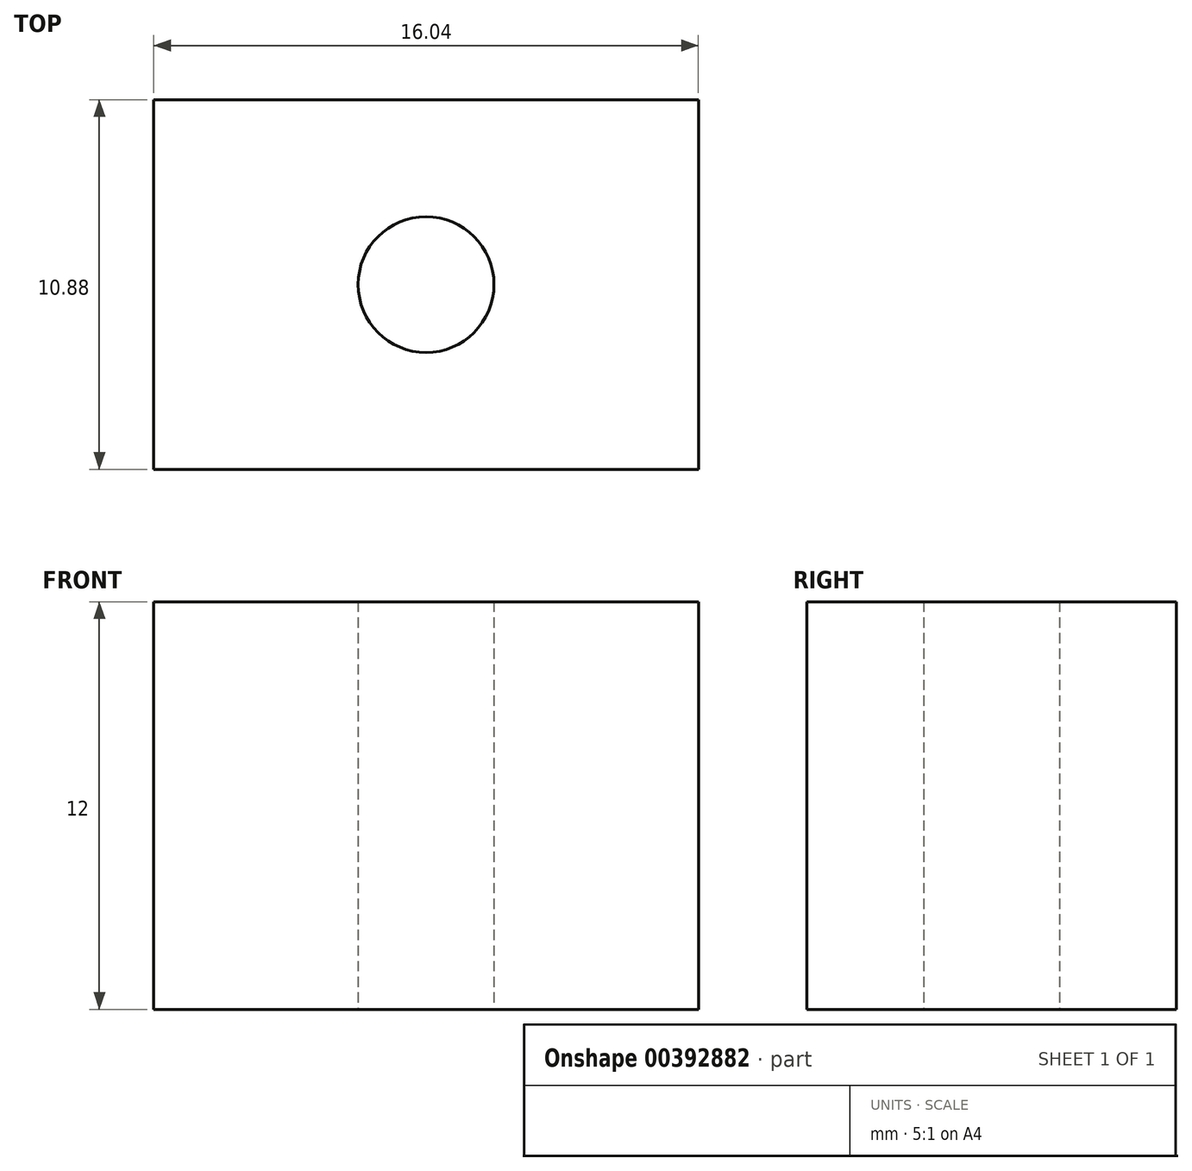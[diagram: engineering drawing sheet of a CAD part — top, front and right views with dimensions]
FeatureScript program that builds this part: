
annotation { "Feature Type Name" : "Feature", "Feature Type Description" : "" }
export const myFeature = defineFeature(function(context is Context, id is Id, definition is map)
    precondition{}
    {
        {
            var Q0;
            Q0=qCreatedBy(makeId("Top.planeOp"),FACE);
            var sketch = newSketch(context, id + "F0", { "sketchPlane" : qUnion([Q0])});
            skCircle(sketch, "E0", {"center": v(0, 0) * mm, "radius": 19.05 * mm});
            skCircle(sketch, "E1", {"center": v(0, 0) * mm, "radius": 7.94 * mm});
            skSolve(sketch);
        }
        {
            var Q0;
            Q0 = qSketchRegion(id + "F0", true);
            extrude(context, id + "F1", {"entities" : qUnion([Q0]), "depth" : 25.4 * mm, "offsetDistance" : 25.4 * mm});
        }
        {
            var Q0;
            Q0=makeQuery(id+"F1.opExtrude","SWEPT_BODY",BODY,{"disambiguationData":[OSD([sQuery(id+"F0.wireOp",EDGE,"E0"),sQuery(id+"F0.wireOp",EDGE,"E1")])]});
            deleteBodies(context, id + "F2", {"entities" : qUnion([Q0])});
        }
        {
            var Q0;
            Q0=qCreatedBy(makeId("Top.planeOp"),FACE);
            var sketch = newSketch(context, id + "F3", { "sketchPlane" : qUnion([Q0])});
            skCircle(sketch, "E2", {"center": v(0, 0) * mm, "radius": 2 * mm});
            skLineSegment(sketch, "E3.bottom", {"start": v(8.02, 5.44) * mm, "end": v(-8.02, 5.44) * mm});
            skLineSegment(sketch, "E3.top", {"start": v(8.02, -5.44) * mm, "end": v(-8.02, -5.44) * mm});
            skLineSegment(sketch, "E3.left", {"start": v(8.02, 5.44) * mm, "end": v(8.02, -5.44) * mm});
            skLineSegment(sketch, "E3.right", {"start": v(-8.02, 5.44) * mm, "end": v(-8.02, -5.44) * mm});
            skSolve(sketch);
        }
        {
            var Q0;
            Q0 = qSketchRegion(id + "F3", true);
            extrude(context, id + "F4", {"entities" : qUnion([Q0]), "depth" : 6 * mm, "offsetDistance" : 25.4 * mm, "hasSecondDirection" : true, "secondDirectionOppositeDirection" : true, "secondDirectionDepth" : 6 * mm});
        }
        {
            var Q0;
            Q0=makeQuery(id+"F4.opExtrude","CAP_FACE",FACE,{"disambiguationData":[OSD([sQuery(id+"F3.wireOp",EDGE,"E2"),sQuery(id+"F3.wireOp",EDGE,"E3.bottom"),sQuery(id+"F3.wireOp",EDGE,"E3.top"),sQuery(id+"F3.wireOp",EDGE,"E3.left"),sQuery(id+"F3.wireOp",EDGE,"E3.right")])],"isStart":true});
            var sketch = newSketch(context, id + "F5", { "sketchPlane" : qUnion([Q0])});
            skCircle(sketch, "E4.0", {"center": v(0, 0) * mm, "radius": 2 * mm});
            skSolve(sketch);
        }
        {
            var Q0;
            Q0=sQuery(id+"F5.wireOp",EDGE,"E4.0");
            extrude(context, id + "F6", {"bodyType" : ToolBodyType.SURFACE, "surfaceEntities" : qUnion([Q0]), "depth" : 25.4 * mm, "offsetDistance" : 25.4 * mm, "hasSecondDirection" : true, "secondDirectionOppositeDirection" : true, "secondDirectionDepth" : 25.4 * mm});
        }
    });
